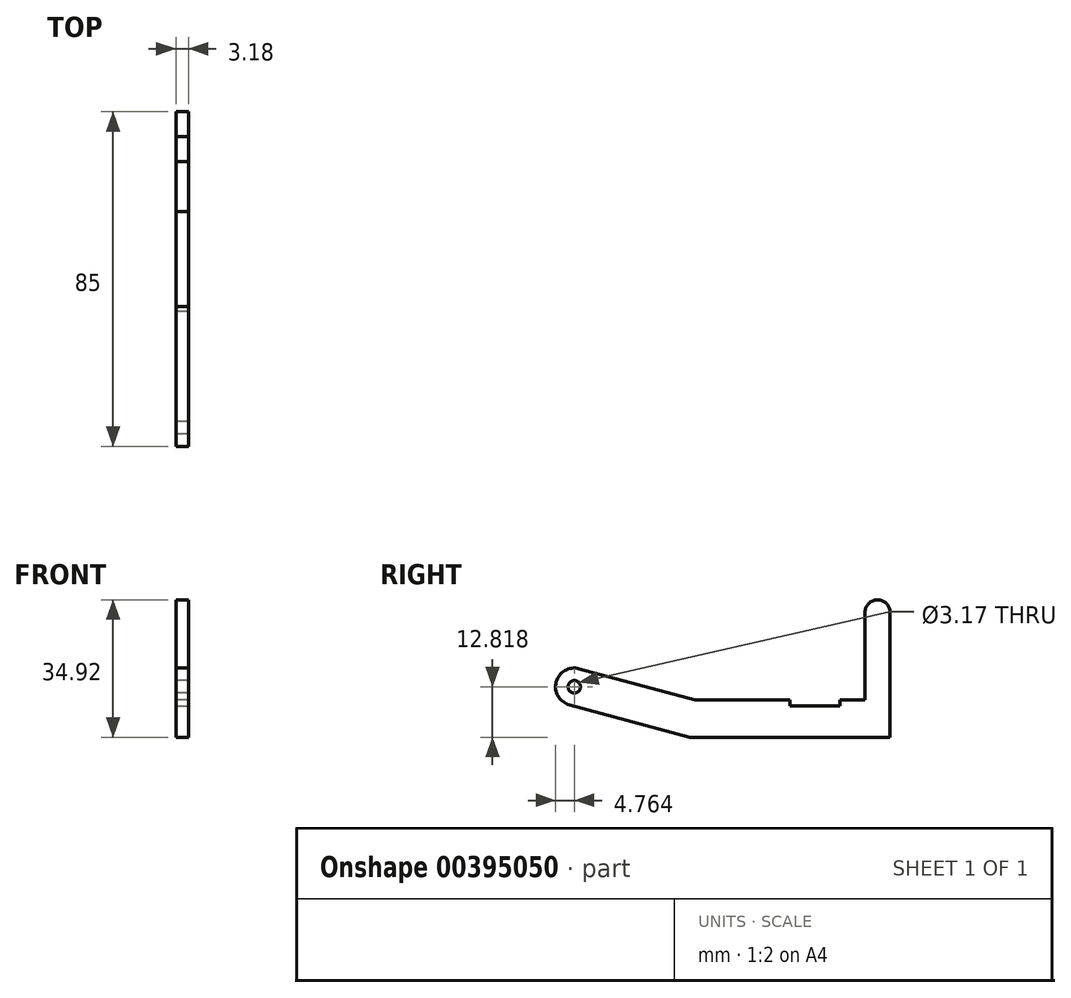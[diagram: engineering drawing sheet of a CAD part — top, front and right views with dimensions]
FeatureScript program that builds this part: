
annotation { "Feature Type Name" : "Feature", "Feature Type Description" : "" }
export const myFeature = defineFeature(function(context is Context, id is Id, definition is map)
    precondition{}
    {
        {
            var Q0;
            Q0=qCreatedBy(makeId("Right.planeOp"),FACE);
            var sketch = newSketch(context, id + "F0", { "sketchPlane" : qUnion([Q0])});
            skLineSegment(sketch, "E0.top", {"start": v(-25.4, 12.7) * mm, "end": v(25.4, 12.7) * mm});
            skLineSegment(sketch, "E1", {"start": v(25.4, 12.7) * mm, "end": v(25.4, 44.45) * mm});
            skLineSegment(sketch, "E2", {"start": v(19.05, 44.45) * mm, "end": v(19.05, 22.22) * mm});
            skLineSegment(sketch, "E3", {"start": v(-24.15, 22.23) * mm, "end": v(19.05, 22.22) * mm});
            skArc(sketch, "E4", {"start": v(25.4, 44.45) * mm, "mid": v(22.22, 47.62) * mm, "end": v(19.05, 44.45) * mm});
            skLineSegment(sketch, "E5", {"start": v(-56.07, 20.92) * mm, "end": v(-25.4, 12.7) * mm});
            skLineSegment(sketch, "E6", {"start": v(-53.6, 30.12) * mm, "end": v(-24.15, 22.23) * mm});
            skArc(sketch, "E7", {"start": v(-53.6, 30.12) * mm, "mid": v(-59.44, 26.75) * mm, "end": v(-56.07, 20.92) * mm});
            skSolve(sketch);
        }
        {
            var Q0;
            Q0=qCreatedBy(makeId("Right.planeOp"),FACE);
            var sketch = newSketch(context, id + "F1", { "sketchPlane" : qUnion([Q0])});
            skCircle(sketch, "E8", {"center": v(-54.84, 25.52) * mm, "radius": 1.59 * mm});
            skSolve(sketch);
        }
        {
            var Q0;
            Q0=qCreatedBy(makeId("Right.planeOp"),FACE);
            var sketch = newSketch(context, id + "F2", { "sketchPlane" : qUnion([Q0])});
            skLineSegment(sketch, "E9.bottom", {"start": v(12.7, 20.64) * mm, "end": v(0, 20.64) * mm});
            skLineSegment(sketch, "E9.top", {"start": v(12.7, 23.81) * mm, "end": v(0, 23.81) * mm});
            skLineSegment(sketch, "E9.left", {"start": v(12.7, 20.64) * mm, "end": v(12.7, 23.81) * mm});
            skLineSegment(sketch, "E9.right", {"start": v(0, 20.64) * mm, "end": v(0, 23.81) * mm});
            skSolve(sketch);
        }
        {
            var Q0;
            Q0=makeQuery(id+"F0.imprint","IMPRINT",FACE,{"disambiguationData":[TD([[makeQuery(id+"F0.imprint","IMPRINT",EDGE,{"derivedFrom":sQuery(id+"F0.wireOp",EDGE,"E0.top")}),1.0]])]});
            extrude(context, id + "F3", {"entities" : qUnion([Q0]), "endBound" : BoundingType.SYMMETRIC, "depth" : 3.17 * mm});
        }
        {
            var Q0;
            Q0 = qSketchRegion(id + "F2", true);
            extrude(context, id + "F4", {"entities" : qUnion([Q0]), "operationType" : NewBodyOperationType.REMOVE, "endBound" : BoundingType.SYMMETRIC, "oppositeDirection" : true, "depth" : 25.4 * mm});
        }
        {
            var Q0;
            Q0 = qSketchRegion(id + "F1", true);
            extrude(context, id + "F5", {"entities" : qUnion([Q0]), "operationType" : NewBodyOperationType.REMOVE, "endBound" : BoundingType.SYMMETRIC, "depth" : 25.4 * mm});
        }
    });
